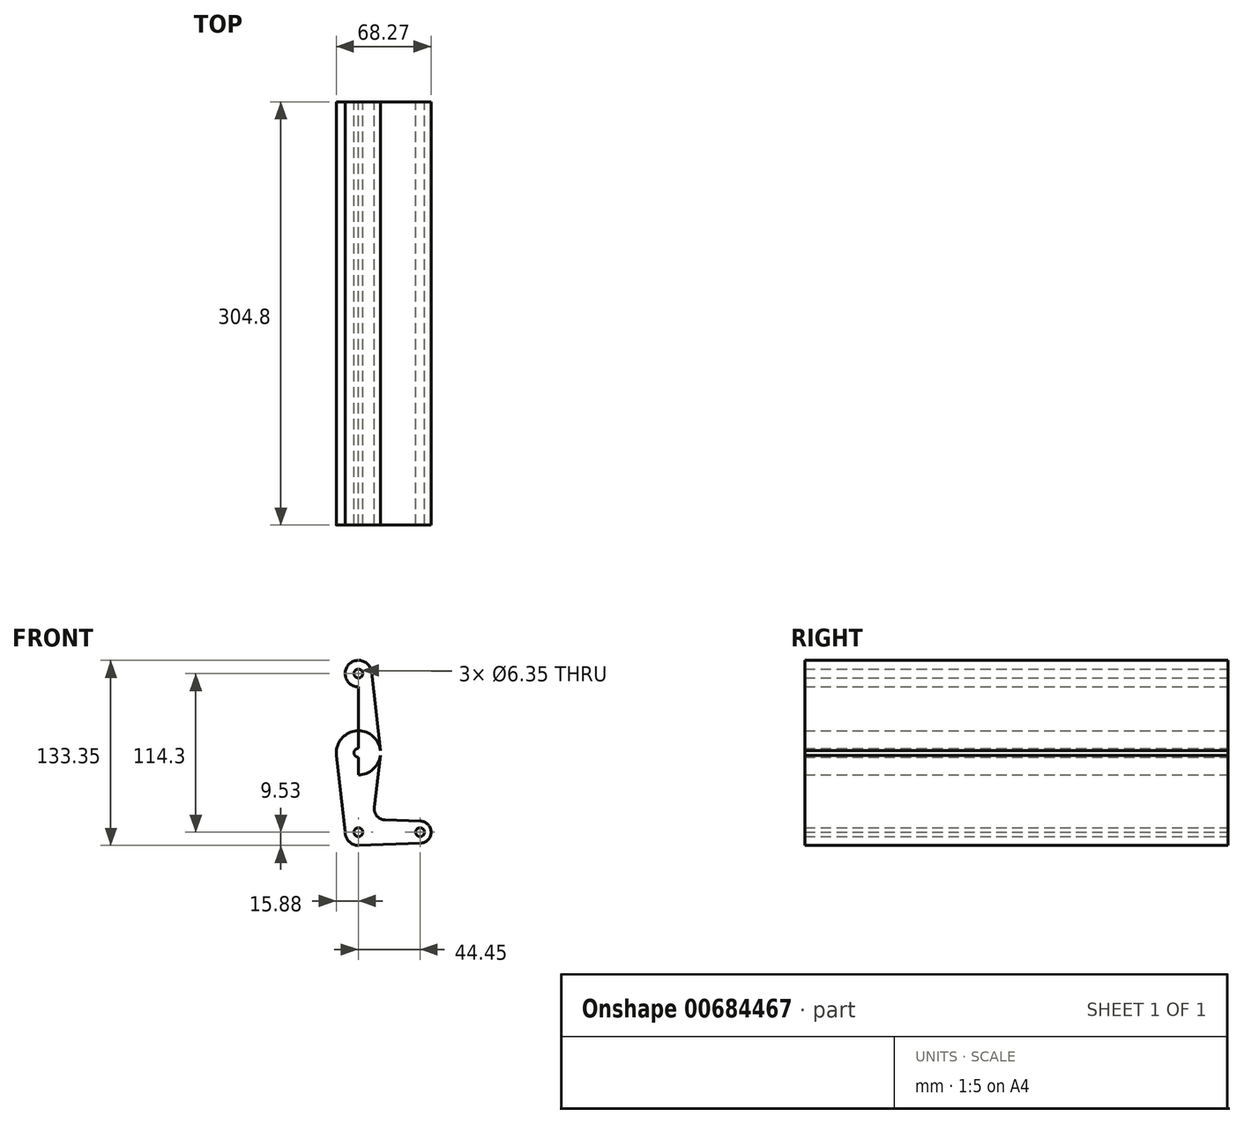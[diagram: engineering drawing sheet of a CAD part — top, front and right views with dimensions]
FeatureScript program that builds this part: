
annotation { "Feature Type Name" : "Feature", "Feature Type Description" : "" }
export const myFeature = defineFeature(function(context is Context, id is Id, definition is map)
    precondition{}
    {
        {
            var Q0;
            Q0=qCreatedBy(makeId("Front.planeOp"),FACE);
            var sketch = newSketch(context, id + "F0", { "sketchPlane" : qUnion([Q0])});
            skLineSegment(sketch, "E0", {"start": v(0, -45.45) * mm, "end": v(0, 68.85) * mm});
            skLineSegment(sketch, "E1", {"start": v(0, -45.45) * mm, "end": v(44.45, -45.45) * mm});
            skCircle(sketch, "E2", {"center": v(0, 68.85) * mm, "radius": 9.53 * mm});
            skCircle(sketch, "E3", {"center": v(44.45, -45.45) * mm, "radius": 7.94 * mm});
            skCircle(sketch, "E4", {"center": v(0, 11.7) * mm, "radius": 15.88 * mm});
            skCircle(sketch, "E5", {"center": v(0, -45.45) * mm, "radius": 9.53 * mm});
            skLineSegment(sketch, "E6", {"start": v(0, -54.98) * mm, "end": v(44.73, -53.38) * mm});
            skLineSegment(sketch, "E7", {"start": v(19.14, -36.6) * mm, "end": v(44.73, -37.52) * mm});
            skLineSegment(sketch, "E8", {"start": v(-15.83, 12.9) * mm, "end": v(-9.47, 69.86) * mm});
            skLineSegment(sketch, "E9", {"start": v(11.52, -27.77) * mm, "end": v(15.77, 9.92) * mm});
            skLineSegment(sketch, "E10", {"start": v(15.77, 13.48) * mm, "end": v(9.47, 69.9) * mm});
            skLineSegment(sketch, "E11", {"start": v(-9.52, -45.3) * mm, "end": v(-15.77, 9.91) * mm});
            skCircle(sketch, "E12", {"center": v(0, 68.85) * mm, "radius": 3.18 * mm});
            skCircle(sketch, "E13", {"center": v(0, 11.7) * mm, "radius": 3.18 * mm});
            skCircle(sketch, "E14", {"center": v(0, -45.45) * mm, "radius": 3.18 * mm});
            skCircle(sketch, "E15", {"center": v(44.45, -45.45) * mm, "radius": 3.18 * mm});
            skLineSegment(sketch, "E16", {"start": v(0, 11.7) * mm, "end": v(0, 47.81) * mm});
            skCircle(sketch, "E17", {"center": v(-2.62, 47.81) * mm, "radius": 1.59 * mm});
            skArc(sketch, "E18.filletArc", {"start": v(11.52, -27.77) * mm, "mid": v(13.4, -33.85) * mm, "end": v(19.14, -36.6) * mm});
            skSolve(sketch);
        }
        {
            var Q0;
            {var subQ0=sQuery(id+"F0.wireOp",EDGE,"E14");var subQ1=sQuery(id+"F0.wireOp",EDGE,"E0");var subQ2=makeQuery(id+"F0.imprint","INTERSECT",VERTEX,{"derivedFrom":[subQ1,subQ0]});Q0=makeQuery(id+"F0.imprint","IMPRINT",FACE,{"disambiguationData":[TD([[makeQuery(id+"F0.imprint","IMPRINT",EDGE,{"disambiguationData":[TD([[subQ2,-1.0]])],"derivedFrom":subQ1}),-1.0]])]});}
            var Q1;
            {var subQ4=sQuery(id+"F0.wireOp",EDGE,"E0");var subQ6=sQuery(id+"F0.wireOp",EDGE,"E14");var subQ7=makeQuery(id+"F0.imprint","INTERSECT",VERTEX,{"derivedFrom":[subQ4,subQ6]});Q1=makeQuery(id+"F0.imprint","IMPRINT",FACE,{"disambiguationData":[TD([[makeQuery(id+"F0.imprint","IMPRINT",EDGE,{"disambiguationData":[TD([[subQ7,-1.0]])],"derivedFrom":subQ4}),1.0]])]});}
            var Q2;
            {var subQ0=sQuery(id+"F0.wireOp",EDGE,"E3");var subQ1=sQuery(id+"F0.wireOp",EDGE,"E1");var subQ2=makeQuery(id+"F0.imprint","INTERSECT",VERTEX,{"derivedFrom":[subQ1,subQ0]});Q2=makeQuery(id+"F0.imprint","IMPRINT",FACE,{"disambiguationData":[TD([[makeQuery(id+"F0.imprint","IMPRINT",EDGE,{"disambiguationData":[TD([[subQ2,1.0]])],"derivedFrom":subQ1}),-1.0]])]});}
            var Q3;
            {var subQ9=sQuery(id+"F0.wireOp",EDGE,"E7");Q3=makeQuery(id+"F0.imprint","IMPRINT",FACE,{"disambiguationData":[TD([[makeQuery(id+"F0.imprint","IMPRINT",EDGE,{"derivedFrom":subQ9}),-1.0]])]});}
            var Q4;
            {var subQ5=sQuery(id+"F0.wireOp",EDGE,"E11");Q4=makeQuery(id+"F0.imprint","IMPRINT",FACE,{"disambiguationData":[TD([[makeQuery(id+"F0.imprint","IMPRINT",EDGE,{"derivedFrom":subQ5}),-1.0]])]});}
            var Q5;
            Q5=makeQuery(id+"F0.imprint","IMPRINT",FACE,{"disambiguationData":[TD([[makeQuery(id+"F0.imprint","IMPRINT",EDGE,{"derivedFrom":sQuery(id+"F0.wireOp",EDGE,"E17")}),-1.0]])]});
            var Q6;
            {var subQ0=sQuery(id+"F0.wireOp",EDGE,"E10");Q6=makeQuery(id+"F0.imprint","IMPRINT",FACE,{"disambiguationData":[TD([[makeQuery(id+"F0.imprint","IMPRINT",EDGE,{"derivedFrom":subQ0}),1.0]])]});}
            var Q7;
            Q7=makeQuery(id+"F0.imprint","IMPRINT",FACE,{"disambiguationData":[TD([[makeQuery(id+"F0.imprint","IMPRINT",EDGE,{"derivedFrom":sQuery(id+"F0.wireOp",EDGE,"E12")}),-1.0]])]});
            var Q8;
            Q8=makeQuery(id+"F0.imprint","IMPRINT",FACE,{"disambiguationData":[TD([[makeQuery(id+"F0.imprint","IMPRINT",EDGE,{"derivedFrom":sQuery(id+"F0.wireOp",EDGE,"E15")}),-1.0]])]});
            var Q9;
            {var subQ0=sQuery(id+"F0.wireOp",EDGE,"E4");var subQ3=sQuery(id+"F0.wireOp",EDGE,"E0");var subQ4=makeQuery(id+"F0.imprint","INTERSECT",VERTEX,{"derivedFrom":[subQ3,subQ0]});Q9=makeQuery(id+"F0.imprint","IMPRINT",FACE,{"disambiguationData":[TD([[makeQuery(id+"F0.imprint","IMPRINT",EDGE,{"disambiguationData":[TD([[subQ4,-1.0]])],"derivedFrom":subQ3}),-1.0]])]});}
            var Q10;
            {var subQ0=sQuery(id+"F0.wireOp",EDGE,"E4");var subQ2=sQuery(id+"F0.wireOp",EDGE,"E0");var subQ3=makeQuery(id+"F0.imprint","INTERSECT",VERTEX,{"derivedFrom":[subQ2,subQ0]});Q10=makeQuery(id+"F0.imprint","IMPRINT",FACE,{"disambiguationData":[TD([[makeQuery(id+"F0.imprint","IMPRINT",EDGE,{"disambiguationData":[TD([[subQ3,-1.0]])],"derivedFrom":subQ2}),1.0]])]});}
            extrude(context, id + "F1", {"entities" : qUnion([Q0, Q1, Q2, Q3, Q4, Q5, Q6, Q7, Q8, Q9, Q10]), "depth" : 304.8 * mm, "offsetDistance" : 25.4 * mm});
        }
    });
